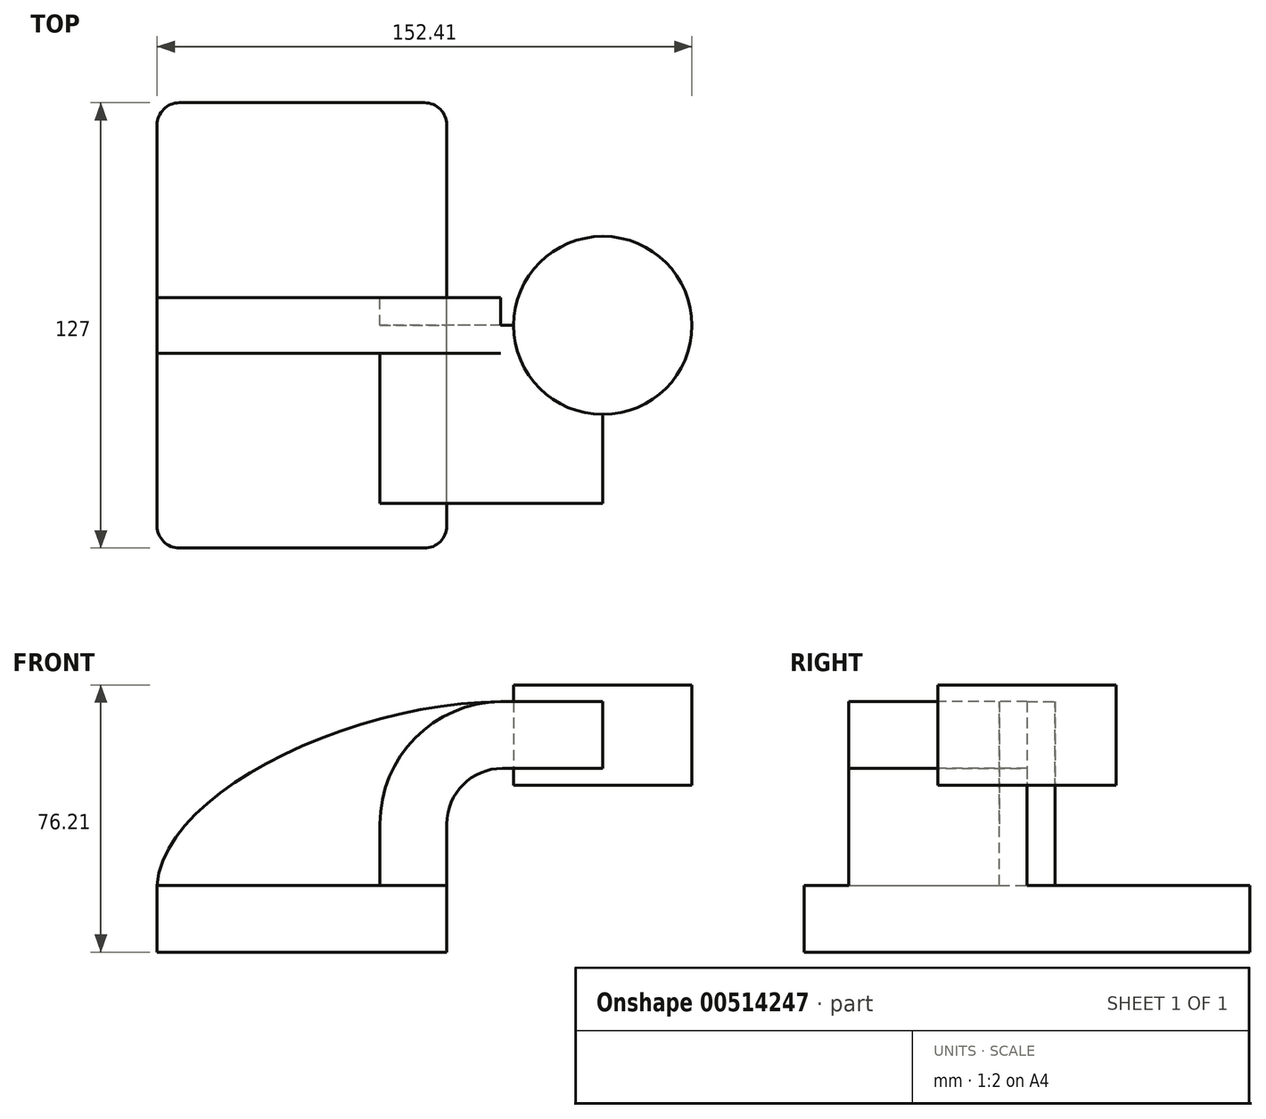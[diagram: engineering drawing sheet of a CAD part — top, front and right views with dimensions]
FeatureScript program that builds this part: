
annotation { "Feature Type Name" : "Feature", "Feature Type Description" : "" }
export const myFeature = defineFeature(function(context is Context, id is Id, definition is map)
    precondition{}
    {
        {
            var Q0;
            Q0=qCreatedBy(makeId("Front.planeOp"),FACE);
            var sketch = newSketch(context, id + "F0", { "sketchPlane" : qUnion([Q0])});
            skLineSegment(sketch, "E0.bottom", {"start": v(-41.28, -9.53) * mm, "end": v(41.28, -9.53) * mm});
            skLineSegment(sketch, "E0.top", {"start": v(-41.28, 9.53) * mm, "end": v(41.28, 9.53) * mm});
            skLineSegment(sketch, "E0.left", {"start": v(-41.28, -9.53) * mm, "end": v(-41.28, 9.53) * mm});
            skLineSegment(sketch, "E0.right", {"start": v(41.28, -9.53) * mm, "end": v(41.28, 9.53) * mm});
            skPoint(sketch, "E0.middle", {"position": v(0, 0) * mm});
            skLineSegment(sketch, "E1.bottom", {"start": v(60.33, 38.1) * mm, "end": v(111.12, 38.1) * mm});
            skLineSegment(sketch, "E1.top", {"start": v(60.33, 66.67) * mm, "end": v(111.12, 66.67) * mm});
            skLineSegment(sketch, "E1.left", {"start": v(60.33, 38.1) * mm, "end": v(60.33, 66.67) * mm});
            skLineSegment(sketch, "E1.right", {"start": v(111.12, 38.1) * mm, "end": v(111.12, 66.67) * mm});
            skPoint(sketch, "E1.middle", {"position": v(85.72, 52.39) * mm});
            skLineSegment(sketch, "E2", {"start": v(41.27, 9.53) * mm, "end": v(41.27, 27) * mm});
            skArc(sketch, "E3", {"start": v(41.27, 27) * mm, "mid": v(45.92, 38.23) * mm, "end": v(57.15, 42.88) * mm});
            skLineSegment(sketch, "E4", {"start": v(57.15, 42.88) * mm, "end": v(85.73, 42.88) * mm});
            skLineSegment(sketch, "E5.0", {"start": v(57.15, 61.93) * mm, "end": v(85.73, 61.93) * mm});
            skArc(sketch, "E5.1", {"start": v(22.23, 27) * mm, "mid": v(32.45, 51.7) * mm, "end": v(57.15, 61.93) * mm});
            skLineSegment(sketch, "E5.2", {"start": v(22.22, 9.53) * mm, "end": v(22.22, 27) * mm});
            skLineSegment(sketch, "E6", {"start": v(85.73, 42.88) * mm, "end": v(85.72, 66.67) * mm});
            skFitSpline(sketch, "E7", {"points": [v(-41.28, 9.52) * mm, v(57.15, 61.93) * mm], "startDerivative": vector(5.66, 80.56) * mm, "endDerivative": vector(128.55, 0.62) * mm});
            skLineSegment(sketch, "E8", {"start": v(85.72, 42.88) * mm, "end": v(85.72, 38.1) * mm});
            skSolve(sketch);
        }
        {
            var Q0;
            Q0=makeQuery(id+"F0.imprint","IMPRINT",FACE,{"disambiguationData":[TD([[makeQuery(id+"F0.imprint","IMPRINT",EDGE,{"derivedFrom":sQuery(id+"F0.wireOp",EDGE,"E0.bottom")}),1.0]])]});
            extrude(context, id + "F1", {"entities" : qUnion([Q0]), "endBound" : BoundingType.SYMMETRIC, "depth" : 127 * mm});
        }
        {
            var Q0;
            {var subQ0=sQuery(id+"F0.wireOp",EDGE,"E4");var subQ1=sQuery(id+"F0.wireOp",EDGE,"E1.left");var subQ2=makeQuery(id+"F0.imprint","INTERSECT",VERTEX,{"derivedFrom":[subQ1,subQ0]});Q0=makeQuery(id+"F0.imprint","IMPRINT",FACE,{"disambiguationData":[TD([[makeQuery(id+"F0.imprint","IMPRINT",EDGE,{"disambiguationData":[TD([[subQ2,-1.0]])],"derivedFrom":subQ1}),-1.0]])]});}
            var Q1;
            {var subQ1=sQuery(id+"F0.wireOp",EDGE,"E2");Q1=makeQuery(id+"F0.imprint","IMPRINT",FACE,{"disambiguationData":[TD([[makeQuery(id+"F0.imprint","IMPRINT",EDGE,{"derivedFrom":subQ1}),1.0]])]});}
            extrude(context, id + "F2", {"entities" : qUnion([Q0, Q1]), "operationType" : NewBodyOperationType.ADD, "depth" : 50.8 * mm});
        }
        {
            var Q0;
            {var subQ3=sQuery(id+"F0.wireOp",EDGE,"E5.2");Q0=makeQuery(id+"F0.imprint","IMPRINT",FACE,{"disambiguationData":[TD([[makeQuery(id+"F0.imprint","IMPRINT",EDGE,{"derivedFrom":subQ3}),1.0]])]});}
            extrude(context, id + "F3", {"entities" : qUnion([Q0]), "operationType" : NewBodyOperationType.ADD, "endBound" : BoundingType.SYMMETRIC, "depth" : 15.88 * mm});
        }
        {
            var Q0;
            {var subQ3=sQuery(id+"F0.wireOp",EDGE,"E1.right");Q0=makeQuery(id+"F0.imprint","IMPRINT",FACE,{"disambiguationData":[TD([[makeQuery(id+"F0.imprint","IMPRINT",EDGE,{"derivedFrom":subQ3}),1.0]])]});}
            var Q1;
            Q1=sQuery(id+"F0.wireOp",EDGE,"E6");
            revolve(context, id + "F4", {"operationType" : NewBodyOperationType.ADD, "entities" : qUnion([Q0]), "axis" : qUnion([Q1]), "revolveType" : RevolveType.FULL});
        }
        {
            var Q0;
            Q0=makeQuery(id+"F1.opExtrude","CAP_EDGE",EDGE,{"disambiguationData":[OSD([sQuery(id+"F0.wireOp",EDGE,"E0.left")])],"isStart":false});
            var Q1;
            Q1=makeQuery(id+"F1.opExtrude","CAP_EDGE",EDGE,{"disambiguationData":[OSD([sQuery(id+"F0.wireOp",EDGE,"E0.right")])],"isStart":false});
            var Q2;
            Q2=makeQuery(id+"F1.opExtrude","CAP_EDGE",EDGE,{"disambiguationData":[OSD([sQuery(id+"F0.wireOp",EDGE,"E0.right")])],"isStart":true});
            fillet(context, id + "F5", {"entities" : qUnion([Q0, Q1, Q2]), "radius" : 6.35 * mm, "tangentPropagation" : true, "allowEdgeOverflow" : false});
        }
        {
            var Q0;
            Q0=makeQuery(id+"F1.opExtrude","CAP_EDGE",EDGE,{"disambiguationData":[OSD([sQuery(id+"F0.wireOp",EDGE,"E0.left")])],"isStart":true});
            fillet(context, id + "F6", {"entities" : qUnion([Q0]), "radius" : 6.35 * mm, "tangentPropagation" : true, "allowEdgeOverflow" : false});
        }
    });
